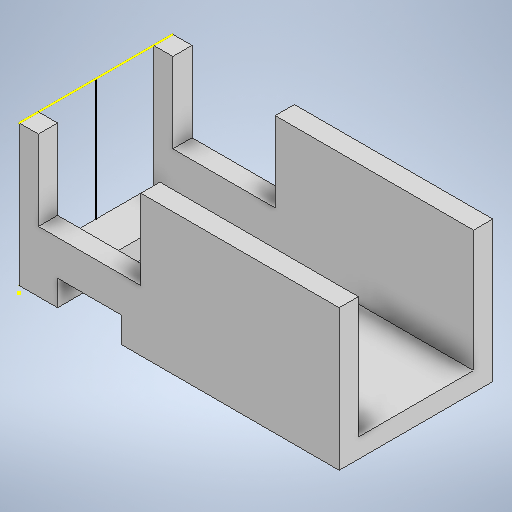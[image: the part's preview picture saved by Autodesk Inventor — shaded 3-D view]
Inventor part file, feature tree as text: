
AUTODESK INVENTOR PART (.ipt)
format: ipt  version: 2025.1 (Build 291241020, 241B)  size: 300,032 bytes
history: native  units: in
note: dims shown in document units (in); Inventor stores cm internally (conversion verified against a paired STEP export)
features: sketch x9, extrude x8
ambient origin geometry x8: Origin, YZ Plane, XZ Plane, XY Plane, X Axis, Y Axis, Z Axis, Center Point
bodies: Body1 (feature_tree)
feature tree (17):
  extrude  "Extrusion2"  Depth=0.9449in
  extrude  "Extrusion3"  Depth=1.378in
  extrude  "Extrusion4"  Depth=0.7087in TaperAngle=0.0deg
  extrude  "Extrusion5"  Depth=0.0394in TaperAngle=0.0deg
  sketch  "Sketch7"  dims[d18=0.5906in d19=0.0in d20=0.1181in]
  extrude  "Extrusion6"  Depth=0.1181in
  extrude  "Extrusion7"  Depth=0.7087in
  extrude  "Extrusion8"  Depth=0.1181in
  extrude  "Extrusion10"  Depth=0.4921in
  sketch  "Sketch3"  dims[d7=1.378in d8=0.9449in]
  sketch  "Sketch4"  dims[d9=0.9055in d10=0.0in d11=1.378in]
  sketch  "Sketch5"  dims[d12=0.7087in d13=0.7874in d14=0.0in]
  sketch  "Sketch6"  dims[d15=0.0394in d16=1.9749in d17=0.0in]
  sketch  "Sketch8"  dims[d21=0.5906in d22=0.0in d23=0.7087in]
  sketch  "Sketch9"  dims[d24=0.3937in d25=0.0in d26=0.1181in]
  sketch  "Sketch10"  dims[d27=0.6299in d28=0.4921in]
  sketch  "Sketch12"  dims[d29=1.2062in d30=0.0in d34=0.2362in d35=0.315in d36=0.0787in d37=0.0787in d38=0.3937in d39=0.0in]
